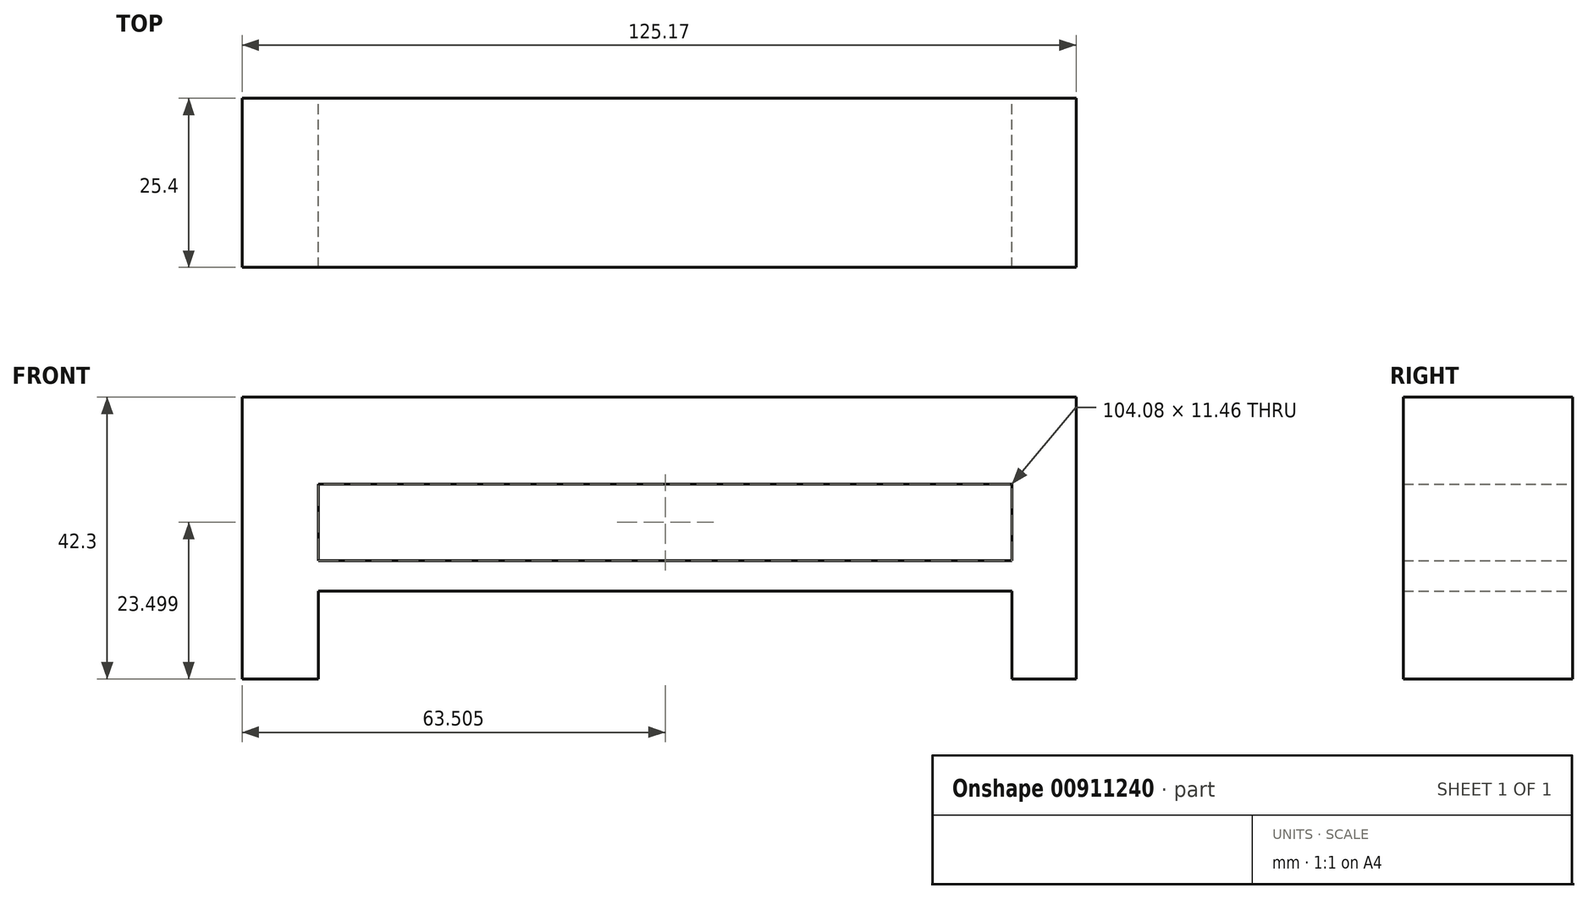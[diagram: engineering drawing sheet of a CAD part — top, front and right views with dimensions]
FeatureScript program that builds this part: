
annotation { "Feature Type Name" : "Feature", "Feature Type Description" : "" }
export const myFeature = defineFeature(function(context is Context, id is Id, definition is map)
    precondition{}
    {
        {
            var Q0;
            Q0=qCreatedBy(makeId("Front.planeOp"),FACE);
            var sketch = newSketch(context, id + "F0", { "sketchPlane" : qUnion([Q0])});
            skLineSegment(sketch, "E0.bottom", {"start": v(-76.69, 42.3) * mm, "end": v(27.4, 42.3) * mm});
            skLineSegment(sketch, "E0.top", {"start": v(-76.69, 29.23) * mm, "end": v(27.4, 29.23) * mm});
            skLineSegment(sketch, "E0.left", {"start": v(-76.69, 42.3) * mm, "end": v(-76.69, 29.23) * mm});
            skLineSegment(sketch, "E0.right", {"start": v(27.4, 42.3) * mm, "end": v(27.4, 29.23) * mm});
            skLineSegment(sketch, "E1.bottom", {"start": v(37.02, 0) * mm, "end": v(27.4, 0) * mm});
            skLineSegment(sketch, "E1.top", {"start": v(37.02, 42.3) * mm, "end": v(27.4, 42.3) * mm});
            skLineSegment(sketch, "E1.left", {"start": v(37.02, 0) * mm, "end": v(37.02, 42.3) * mm});
            skLineSegment(sketch, "E1.right", {"start": v(27.4, 0) * mm, "end": v(27.4, 42.3) * mm});
            skLineSegment(sketch, "E2.bottom", {"start": v(-76.69, 0) * mm, "end": v(-88.15, 0) * mm});
            skLineSegment(sketch, "E2.top", {"start": v(-76.69, 42.3) * mm, "end": v(-88.15, 42.3) * mm});
            skLineSegment(sketch, "E2.left", {"start": v(-76.69, 0) * mm, "end": v(-76.69, 42.3) * mm});
            skLineSegment(sketch, "E2.right", {"start": v(-88.15, 0) * mm, "end": v(-88.15, 42.3) * mm});
            skLineSegment(sketch, "E3.bottom", {"start": v(27.4, 17.77) * mm, "end": v(-76.69, 17.77) * mm});
            skLineSegment(sketch, "E3.top", {"start": v(27.4, 13.18) * mm, "end": v(-76.69, 13.18) * mm});
            skLineSegment(sketch, "E3.left", {"start": v(27.4, 17.77) * mm, "end": v(27.4, 13.18) * mm});
            skLineSegment(sketch, "E3.right", {"start": v(-76.69, 17.77) * mm, "end": v(-76.69, 13.18) * mm});
            skSolve(sketch);
        }
        {
            var Q0;
            {var subQ1=sQuery(id+"F0.wireOp",EDGE,"E1.bottom");Q0=makeQuery(id+"F0.imprint","IMPRINT",FACE,{"disambiguationData":[TD([[makeQuery(id+"F0.imprint","IMPRINT",EDGE,{"derivedFrom":subQ1}),-1.0]])]});}
            var Q1;
            {var subQ0=sQuery(id+"F0.wireOp",EDGE,"E0.bottom");Q1=makeQuery(id+"F0.imprint","IMPRINT",FACE,{"disambiguationData":[TD([[makeQuery(id+"F0.imprint","IMPRINT",EDGE,{"derivedFrom":subQ0}),-1.0]])]});}
            var Q2;
            {var subQ3=sQuery(id+"F0.wireOp",EDGE,"E2.bottom");Q2=makeQuery(id+"F0.imprint","IMPRINT",FACE,{"disambiguationData":[TD([[makeQuery(id+"F0.imprint","IMPRINT",EDGE,{"derivedFrom":subQ3}),-1.0]])]});}
            var Q3;
            Q3=makeQuery(id+"F0.imprint","IMPRINT",FACE,{"disambiguationData":[TD([[makeQuery(id+"F0.imprint","IMPRINT",EDGE,{"derivedFrom":sQuery(id+"F0.wireOp",EDGE,"E3.bottom")}),1.0]])]});
            extrude(context, id + "F1", {"entities" : qUnion([Q0, Q1, Q2, Q3]), "depth" : 25.4 * mm, "offsetDistance" : 25.4 * mm});
        }
    });
